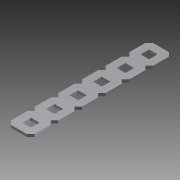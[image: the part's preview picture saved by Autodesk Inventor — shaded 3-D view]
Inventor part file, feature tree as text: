
AUTODESK INVENTOR PART (.ipt)
format: ipt  version: 2014 SP1 (Build 180222100, 222)  size: 491,008 bytes
history: native  units: in
note: dims shown in document units (in); Inventor stores cm internally (conversion verified against a paired STEP export)
features: other x1, imported_body x1, extrude x1, sketch x1
ambient origin geometry x8: Origin, YZ Plane, XZ Plane, XY Plane, X Axis, Y Axis, Z Axis, Center Point
bodies: Body1 (feature_tree)
feature tree (4):
  parser-record x1  (decoder bookkeeping rows leaked as tree rows — omitted from the tree; the rows remain in map.json)
  imported_body  "Base1"
  extrude  "Extrusion1"  Depth=1.0in TaperAngle=0.0deg
  sketch  "Sketch1"  dims[d0=3.0in d1=1.0in d2=0.0in]
